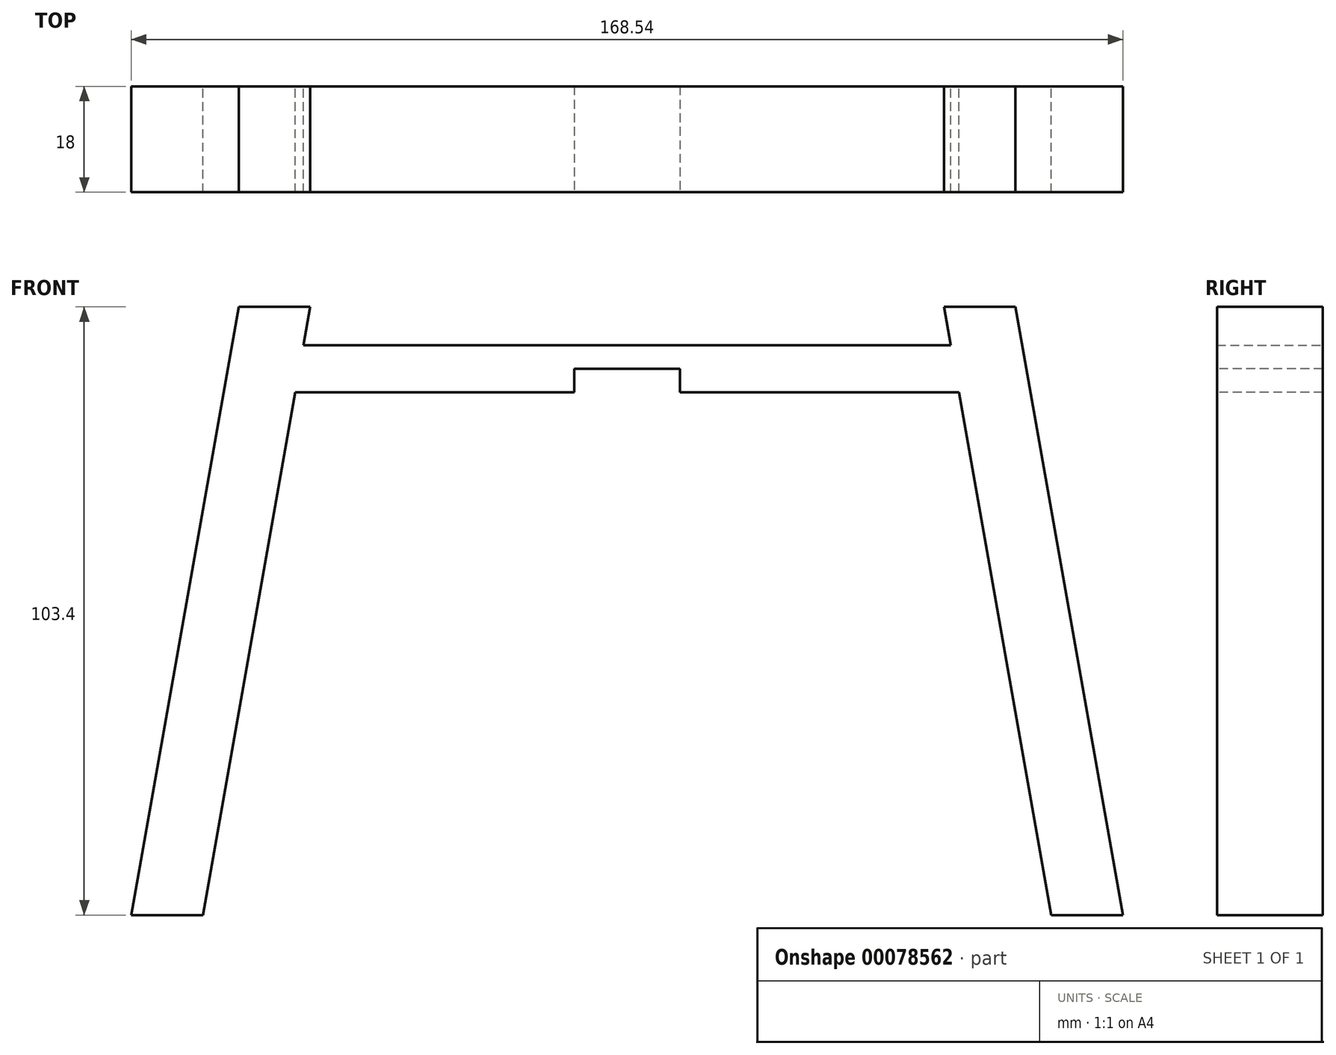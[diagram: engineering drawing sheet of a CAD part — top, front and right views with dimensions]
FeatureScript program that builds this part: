
annotation { "Feature Type Name" : "Feature", "Feature Type Description" : "" }
export const myFeature = defineFeature(function(context is Context, id is Id, definition is map)
    precondition{}
    {
        {
            var Q0;
            Q0=qCreatedBy(makeId("Front.planeOp"),FACE);
            var sketch = newSketch(context, id + "F0", { "sketchPlane" : qUnion([Q0])});
            skLineSegment(sketch, "E0", {"start": v(0, 96.9) * mm, "end": v(-55, 96.9) * mm});
            skLineSegment(sketch, "E1", {"start": v(-55, 96.9) * mm, "end": v(-53.85, 103.4) * mm});
            skLineSegment(sketch, "E2", {"start": v(-53.85, 103.4) * mm, "end": v(-66.04, 103.4) * mm});
            skLineSegment(sketch, "E3", {"start": v(-66.04, 103.4) * mm, "end": v(-84.27, 0) * mm});
            skLineSegment(sketch, "E4", {"start": v(-84.27, 0) * mm, "end": v(-72.09, 0) * mm});
            skLineSegment(sketch, "E5", {"start": v(-72.09, 0) * mm, "end": v(-56.41, 88.9) * mm});
            skLineSegment(sketch, "E6", {"start": v(-56.41, 88.9) * mm, "end": v(0, 88.9) * mm});
            skLineSegment(sketch, "E7", {"start": v(0, 88.9) * mm, "end": v(0, 96.9) * mm, "construction": true});
            skLineSegment(sketch, "E8.MirrorCS", {"start": v(55, 96.9) * mm, "end": v(53.85, 103.4) * mm});
            skLineSegment(sketch, "E9.MirrorCS", {"start": v(66.04, 103.4) * mm, "end": v(84.27, 0) * mm});
            skLineSegment(sketch, "E10.MirrorCS", {"start": v(56.41, 88.9) * mm, "end": v(0, 88.9) * mm});
            skLineSegment(sketch, "E11.MirrorCS", {"start": v(84.27, 0) * mm, "end": v(72.09, 0) * mm});
            skLineSegment(sketch, "E12.MirrorCS", {"start": v(53.85, 103.4) * mm, "end": v(66.04, 103.4) * mm});
            skLineSegment(sketch, "E13.MirrorCS", {"start": v(0, 96.9) * mm, "end": v(55, 96.9) * mm});
            skLineSegment(sketch, "E14.MirrorCS", {"start": v(72.09, 0) * mm, "end": v(56.41, 88.9) * mm});
            skSolve(sketch);
        }
        {
            var Q0;
            Q0=makeQuery(id+"F0.imprint","IMPRINT",FACE,{"disambiguationData":[TD([[makeQuery(id+"F0.imprint","IMPRINT",EDGE,{"derivedFrom":sQuery(id+"F0.wireOp",EDGE,"E0")}),1.0]])]});
            extrude(context, id + "F1", {"entities" : qUnion([Q0]), "depth" : 18 * mm});
        }
        {
            var Q0;
            Q0=makeQuery(id+"F1.opExtrude","CAP_FACE",FACE,{"disambiguationData":[OSD([sQuery(id+"F0.wireOp",EDGE,"E0"),sQuery(id+"F0.wireOp",EDGE,"E1"),sQuery(id+"F0.wireOp",EDGE,"E2"),sQuery(id+"F0.wireOp",EDGE,"E3"),sQuery(id+"F0.wireOp",EDGE,"E4"),sQuery(id+"F0.wireOp",EDGE,"E5"),sQuery(id+"F0.wireOp",EDGE,"E6"),sQuery(id+"F0.wireOp",EDGE,"E8.MirrorCS"),sQuery(id+"F0.wireOp",EDGE,"E9.MirrorCS"),sQuery(id+"F0.wireOp",EDGE,"E10.MirrorCS"),sQuery(id+"F0.wireOp",EDGE,"E11.MirrorCS"),sQuery(id+"F0.wireOp",EDGE,"E12.MirrorCS"),sQuery(id+"F0.wireOp",EDGE,"E13.MirrorCS"),sQuery(id+"F0.wireOp",EDGE,"E14.MirrorCS")])],"isStart":false});
            var sketch = newSketch(context, id + "F2", { "sketchPlane" : qUnion([Q0])});
            skLineSegment(sketch, "E15.bottom", {"start": v(-9, 88.9) * mm, "end": v(9, 88.9) * mm});
            skLineSegment(sketch, "E15.top", {"start": v(-9, 92.9) * mm, "end": v(9, 92.9) * mm});
            skLineSegment(sketch, "E15.left", {"start": v(-9, 88.9) * mm, "end": v(-9, 92.9) * mm});
            skLineSegment(sketch, "E15.right", {"start": v(9, 88.9) * mm, "end": v(9, 92.9) * mm});
            skSolve(sketch);
        }
        {
            var Q0;
            Q0=makeQuery(id+"F2.imprint","IMPRINT",FACE,{"disambiguationData":[TD([[makeQuery(id+"F2.imprint","IMPRINT",EDGE,{"derivedFrom":sQuery(id+"F2.wireOp",EDGE,"E15.bottom")}),1.0]])]});
            extrude(context, id + "F3", {"entities" : qUnion([Q0]), "operationType" : NewBodyOperationType.REMOVE, "oppositeDirection" : true, "depth" : 20 * mm});
        }
    });
